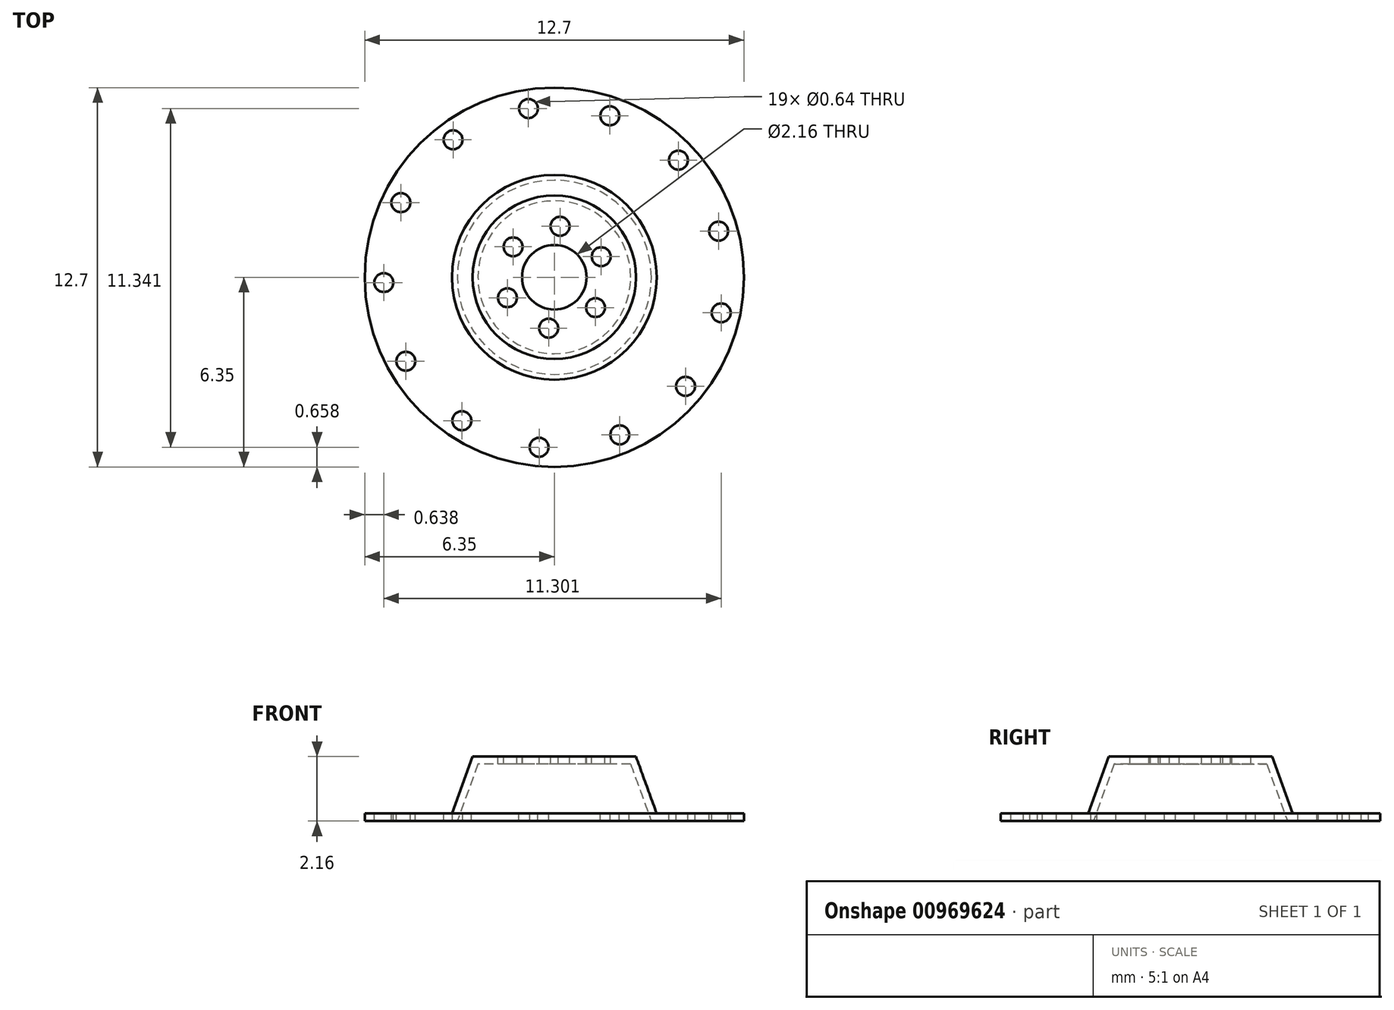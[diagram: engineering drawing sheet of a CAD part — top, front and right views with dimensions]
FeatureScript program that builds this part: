
annotation { "Feature Type Name" : "Feature", "Feature Type Description" : "" }
export const myFeature = defineFeature(function(context is Context, id is Id, definition is map)
    precondition{}
    {
        {
            var Q0;
            Q0=qCreatedBy(makeId("Top.planeOp"),FACE);
            var sketch = newSketch(context, id + "F0", { "sketchPlane" : qUnion([Q0])});
            skCircle(sketch, "E0", {"center": v(0, 0) * mm, "radius": 6.35 * mm});
            skSolve(sketch);
        }
        {
            var Q0;
            Q0=makeQuery(id+"F0.imprint","IMPRINT",FACE,{"disambiguationData":[TD([[makeQuery(id+"F0.imprint","IMPRINT",EDGE,{"derivedFrom":sQuery(id+"F0.wireOp",EDGE,"E0")}),1.0]])]});
            extrude(context, id + "F1", {"entities" : qUnion([Q0]), "depth" : 0.25 * mm, "offsetDistance" : 25.4 * mm});
        }
        {
            var Q0;
            Q0=makeQuery(id+"F1.opExtrude","CAP_FACE",FACE,{"disambiguationData":[OSD([sQuery(id+"F0.wireOp",EDGE,"E0")])],"isStart":false});
            var sketch = newSketch(context, id + "F2", { "sketchPlane" : qUnion([Q0])});
            skCircle(sketch, "E1", {"center": v(0, 0) * mm, "radius": 3.43 * mm});
            skSolve(sketch);
        }
        {
            var Q0;
            Q0=makeQuery(id+"F2.imprint","IMPRINT",FACE,{"disambiguationData":[TD([[makeQuery(id+"F2.imprint","IMPRINT",EDGE,{"derivedFrom":sQuery(id+"F2.wireOp",EDGE,"E1")}),1.0]])]});
            extrude(context, id + "F3", {"entities" : qUnion([Q0]), "operationType" : NewBodyOperationType.ADD, "depth" : 1.9 * mm, "offsetDistance" : 25.4 * mm, "hasDraft" : true, "draftAngle" : 20 * degree, "draftPullDirection" : true});
        }
        {
            var Q0;
            Q0=makeQuery(id+"F1.opExtrude","CAP_FACE",FACE,{"disambiguationData":[OSD([sQuery(id+"F0.wireOp",EDGE,"E0")])],"isStart":true});
            shell(context, id + "F4", {"entities" : qUnion([Q0]), "thickness" : 0.25 * mm});
        }
        {
            var Q0;
            Q0=makeQuery(id+"F3.opExtrude","CAP_FACE",FACE,{"disambiguationData":[OSD([sQuery(id+"F2.wireOp",EDGE,"E1")])],"isStart":false});
            var sketch = newSketch(context, id + "F5", { "sketchPlane" : qUnion([Q0])});
            skCircle(sketch, "E2", {"center": v(0, 0) * mm, "radius": 1.08 * mm});
            skSolve(sketch);
        }
        {
            var Q0;
            Q0=makeQuery(id+"F5.imprint","IMPRINT",FACE,{"disambiguationData":[TD([[makeQuery(id+"F5.imprint","IMPRINT",EDGE,{"derivedFrom":sQuery(id+"F5.wireOp",EDGE,"E2")}),1.0]])]});
            extrude(context, id + "F6", {"entities" : qUnion([Q0]), "operationType" : NewBodyOperationType.REMOVE, "oppositeDirection" : true, "depth" : 25.4 * mm, "offsetDistance" : 25.4 * mm});
        }
        {
            var Q0;
            Q0=makeQuery(id+"F3.opExtrude","CAP_FACE",FACE,{"disambiguationData":[OSD([sQuery(id+"F2.wireOp",EDGE,"E1")])],"isStart":false});
            var sketch = newSketch(context, id + "F7", { "sketchPlane" : qUnion([Q0])});
            skCircle(sketch, "E3", {"center": v(-1.38, 1.02) * mm, "radius": 0.32 * mm});
            skCircle(sketch, "E4.1.0", {"center": v(-1.57, -0.69) * mm, "radius": 0.32 * mm});
            skCircle(sketch, "E4.2.0", {"center": v(-0.2, -1.7) * mm, "radius": 0.32 * mm});
            skCircle(sketch, "E4.3.0", {"center": v(1.38, -1.02) * mm, "radius": 0.32 * mm});
            skCircle(sketch, "E4.4.0", {"center": v(1.57, 0.69) * mm, "radius": 0.32 * mm});
            skCircle(sketch, "E4.5.0", {"center": v(0.2, 1.7) * mm, "radius": 0.32 * mm});
            skPoint(sketch, "E4.center", {"position": v(0, 0) * mm});
            skSolve(sketch);
        }
        {
            var Q0;
            Q0 = qSketchRegion(id + "F7", true);
            extrude(context, id + "F8", {"entities" : qUnion([Q0]), "operationType" : NewBodyOperationType.REMOVE, "oppositeDirection" : true, "depth" : 25.4 * mm, "offsetDistance" : 25.4 * mm});
        }
        {
            var Q0;
            Q0=makeQuery(id+"F1.opExtrude","CAP_FACE",FACE,{"disambiguationData":[OSD([sQuery(id+"F0.wireOp",EDGE,"E0")])],"isStart":false});
            var sketch = newSketch(context, id + "F9", { "sketchPlane" : qUnion([Q0])});
            skCircle(sketch, "E5", {"center": v(-3.4, 4.6) * mm, "radius": 0.32 * mm});
            skCircle(sketch, "E6.1.0", {"center": v(-5.14, 2.5) * mm, "radius": 0.32 * mm});
            skCircle(sketch, "E6.2.0", {"center": v(-5.71, -0.18) * mm, "radius": 0.32 * mm});
            skCircle(sketch, "E6.3.0", {"center": v(-4.97, -2.81) * mm, "radius": 0.32 * mm});
            skCircle(sketch, "E6.4.0", {"center": v(-3.1, -4.8) * mm, "radius": 0.32 * mm});
            skCircle(sketch, "E6.5.0", {"center": v(-0.51, -5.7) * mm, "radius": 0.32 * mm});
            skCircle(sketch, "E6.6.0", {"center": v(2.2, -5.28) * mm, "radius": 0.32 * mm});
            skCircle(sketch, "E6.7.0", {"center": v(4.4, -3.65) * mm, "radius": 0.32 * mm});
            skCircle(sketch, "E6.8.0", {"center": v(5.59, -1.2) * mm, "radius": 0.32 * mm});
            skCircle(sketch, "E6.9.0", {"center": v(5.5, 1.54) * mm, "radius": 0.32 * mm});
            skPoint(sketch, "E6.center", {"position": v(0, 0) * mm});
            skCircle(sketch, "E7.1.10.0", {"center": v(4.16, 3.92) * mm, "radius": 0.32 * mm});
            skCircle(sketch, "E7.1.11.0", {"center": v(1.86, 5.4) * mm, "radius": 0.32 * mm});
            skCircle(sketch, "E7.1.12.0", {"center": v(-0.87, 5.65) * mm, "radius": 0.32 * mm});
            skSolve(sketch);
        }
        {
            var Q0;
            Q0 = qSketchRegion(id + "F9", true);
            extrude(context, id + "F10", {"entities" : qUnion([Q0]), "operationType" : NewBodyOperationType.REMOVE, "oppositeDirection" : true, "depth" : 25.4 * mm, "offsetDistance" : 25.4 * mm});
        }
    });
